# Revit family: EKF_EE_ПередняяЗадняяПанелиСейсмоцоколяTrivia_AVERES
name_source: partatom
category: Электрооборудование
units: mm (PartAtom-declared; Revit-internal decimal feet)

## family parameters
Всегда вертикально = Нет
На основе рабочей плоскости = Да
Общий = Да
При загрузке вырезать с полостями = Нет
Размер круглого соединителя = Использовать диаметр
Тип детали = Силовой щит
Точка расчета площади = Нет

## types (2) — shared parameters
1левая = 59 мм
1правая = 59 мм
2левая = 4 мм
2правая = 4 мм
ADSK_Единица измерения = шт.
ADSK_Завод-изготовитель = EKF
ADSK_Количество = 1
ADSK_Размер_Высота = 96 мм
ADSK_Размер_Глубина = 25 мм
t1 = 1.5 мм
t2 = 3 мм
ВнОтверстия = 75 мм
Изготовитель = EKF
Отв = 19 мм
Отметка по умолчанию = 1219.2 мм
Серия номенклатуры = Averes
Степень защиты IP = -
ТВ = EKF_2_TRIVIA_AVERES
Тип установки = -
zero-valued in all types: ADSK_Масса

## per-type parameters (varying)
| type | ADSK_Код изделия | ADSK_Размер_Ширина | Тип | Ширина |
| Передняя и задняя панели сейсмоцоколя Ш600 мм EKF AVERES | BFP600SR | 600 мм | 752 мм | 600 мм |
| Передняя и задняя панели сейсмоцоколя Ш800 мм EKF AVERES | BFP800SR | 800 мм | 753 мм | 800 мм |

note: column(s) folded — value = type name in every type: ADSK_Марка, ADSK_Наименование, ADSK_Обозначение
